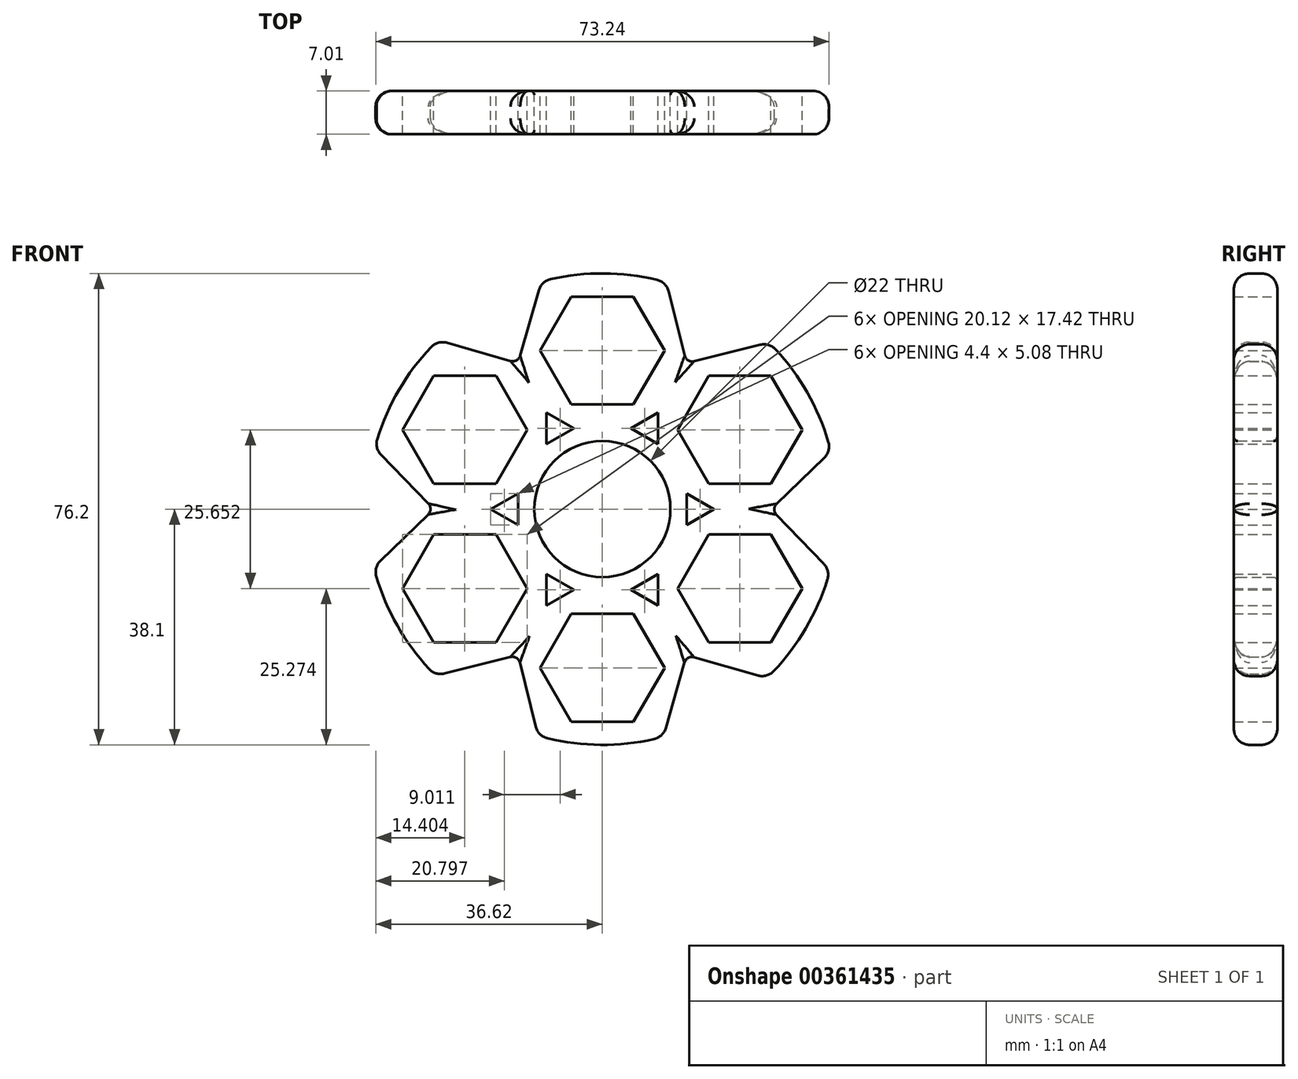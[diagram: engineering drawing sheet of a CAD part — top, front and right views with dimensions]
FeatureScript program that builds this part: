
annotation { "Feature Type Name" : "Feature", "Feature Type Description" : "" }
export const myFeature = defineFeature(function(context is Context, id is Id, definition is map)
    precondition{}
    {
        {
            var Q0;
            Q0=qCreatedBy(makeId("Front.planeOp"),FACE);
            var sketch = newSketch(context, id + "F0", { "sketchPlane" : qUnion([Q0])});
            skCircle(sketch, "E0", {"center": v(0, 0) * mm, "radius": 11 * mm});
            skCircle(sketch, "E1", {"center": v(0, 0) * mm, "radius": 38.1 * mm});
            skLineSegment(sketch, "E2", {"start": v(0, 0) * mm, "end": v(0, 19.86) * mm});
            skCircle(sketch, "E3.cCircle", {"center": v(0, 25.65) * mm, "radius": 8.71 * mm, "construction": true});
            skLineSegment(sketch, "E3.0", {"start": v(5.03, 16.94) * mm, "end": v(-5.03, 16.94) * mm});
            skLineSegment(sketch, "E3.1", {"start": v(-5.03, 16.94) * mm, "end": v(-10.06, 25.65) * mm});
            skLineSegment(sketch, "E3.2", {"start": v(-10.06, 25.65) * mm, "end": v(-5.03, 34.36) * mm});
            skLineSegment(sketch, "E3.3", {"start": v(-5.03, 34.36) * mm, "end": v(5.03, 34.36) * mm});
            skLineSegment(sketch, "E3.4", {"start": v(5.03, 34.36) * mm, "end": v(10.06, 25.65) * mm});
            skLineSegment(sketch, "E3.5", {"start": v(10.06, 25.65) * mm, "end": v(5.03, 16.94) * mm});
            skPoint(sketch, "E3.0.midPoint", {"position": v(0, 16.94) * mm});
            skLineSegment(sketch, "E4.1.0", {"start": v(-32.28, 12.83) * mm, "end": v(-27.25, 21.54) * mm});
            skLineSegment(sketch, "E4.1.1", {"start": v(-27.25, 4.11) * mm, "end": v(-32.28, 12.83) * mm});
            skLineSegment(sketch, "E4.1.2", {"start": v(-17.19, 4.11) * mm, "end": v(-27.25, 4.11) * mm});
            skLineSegment(sketch, "E4.1.3", {"start": v(-12.16, 12.83) * mm, "end": v(-17.19, 4.11) * mm});
            skLineSegment(sketch, "E4.1.4", {"start": v(-17.19, 21.54) * mm, "end": v(-12.16, 12.83) * mm});
            skCircle(sketch, "E4.1.5", {"center": v(-22.22, 12.83) * mm, "radius": 8.71 * mm, "construction": true});
            skLineSegment(sketch, "E4.1.6", {"start": v(-27.25, 21.54) * mm, "end": v(-17.19, 21.54) * mm});
            skLineSegment(sketch, "E4.2.0", {"start": v(-27.25, -21.54) * mm, "end": v(-32.28, -12.83) * mm});
            skLineSegment(sketch, "E4.2.1", {"start": v(-17.19, -21.54) * mm, "end": v(-27.25, -21.54) * mm});
            skLineSegment(sketch, "E4.2.2", {"start": v(-12.16, -12.83) * mm, "end": v(-17.19, -21.54) * mm});
            skLineSegment(sketch, "E4.2.3", {"start": v(-17.19, -4.11) * mm, "end": v(-12.16, -12.83) * mm});
            skLineSegment(sketch, "E4.2.4", {"start": v(-27.25, -4.11) * mm, "end": v(-17.19, -4.11) * mm});
            skCircle(sketch, "E4.2.5", {"center": v(-22.22, -12.83) * mm, "radius": 8.71 * mm, "construction": true});
            skLineSegment(sketch, "E4.2.6", {"start": v(-32.28, -12.83) * mm, "end": v(-27.25, -4.11) * mm});
            skLineSegment(sketch, "E5.1.3.0", {"start": v(5.03, -34.36) * mm, "end": v(-5.03, -34.36) * mm});
            skLineSegment(sketch, "E5.3.3.0", {"start": v(10.06, -25.65) * mm, "end": v(5.03, -34.36) * mm});
            skLineSegment(sketch, "E5.6.3.0", {"start": v(5.03, -16.94) * mm, "end": v(10.06, -25.65) * mm});
            skLineSegment(sketch, "E5.9.3.0", {"start": v(-5.03, -16.94) * mm, "end": v(5.03, -16.94) * mm});
            skLineSegment(sketch, "E5.12.3.0", {"start": v(-10.06, -25.65) * mm, "end": v(-5.03, -16.94) * mm});
            skCircle(sketch, "E5.15.3.0", {"center": v(0, -25.65) * mm, "radius": 8.71 * mm, "construction": true});
            skLineSegment(sketch, "E5.17.3.0", {"start": v(-5.03, -34.36) * mm, "end": v(-10.06, -25.65) * mm});
            skLineSegment(sketch, "E5.1.4.0", {"start": v(32.28, -12.83) * mm, "end": v(27.25, -21.54) * mm});
            skLineSegment(sketch, "E5.3.4.0", {"start": v(27.25, -4.11) * mm, "end": v(32.28, -12.83) * mm});
            skLineSegment(sketch, "E5.6.4.0", {"start": v(17.19, -4.11) * mm, "end": v(27.25, -4.11) * mm});
            skLineSegment(sketch, "E5.9.4.0", {"start": v(12.16, -12.83) * mm, "end": v(17.19, -4.11) * mm});
            skLineSegment(sketch, "E5.12.4.0", {"start": v(17.19, -21.54) * mm, "end": v(12.16, -12.83) * mm});
            skCircle(sketch, "E5.15.4.0", {"center": v(22.22, -12.83) * mm, "radius": 8.71 * mm, "construction": true});
            skLineSegment(sketch, "E5.17.4.0", {"start": v(27.25, -21.54) * mm, "end": v(17.19, -21.54) * mm});
            skLineSegment(sketch, "E6.1.5.0", {"start": v(27.25, 21.54) * mm, "end": v(32.28, 12.83) * mm});
            skLineSegment(sketch, "E6.3.5.0", {"start": v(17.19, 21.54) * mm, "end": v(27.25, 21.54) * mm});
            skLineSegment(sketch, "E6.6.5.0", {"start": v(12.16, 12.83) * mm, "end": v(17.19, 21.54) * mm});
            skLineSegment(sketch, "E6.9.5.0", {"start": v(17.19, 4.11) * mm, "end": v(12.16, 12.83) * mm});
            skLineSegment(sketch, "E6.12.5.0", {"start": v(27.25, 4.11) * mm, "end": v(17.19, 4.11) * mm});
            skCircle(sketch, "E6.15.5.0", {"center": v(22.22, 12.83) * mm, "radius": 8.71 * mm, "construction": true});
            skLineSegment(sketch, "E6.17.5.0", {"start": v(32.28, 12.83) * mm, "end": v(27.25, 4.11) * mm});
            skLineSegment(sketch, "E7", {"start": v(17.19, 21.54) * mm, "end": v(10.06, 25.65) * mm});
            skPoint(sketch, "E8", {"position": v(13.62, 23.6) * mm});
            skLineSegment(sketch, "E9", {"start": v(13.62, 23.6) * mm, "end": v(10.36, 36.66) * mm});
            skLineSegment(sketch, "E10", {"start": v(13.62, 23.6) * mm, "end": v(26.96, 26.92) * mm});
            skLineSegment(sketch, "E11.1.0", {"start": v(-13.62, 23.6) * mm, "end": v(-26.57, 27.3) * mm});
            skLineSegment(sketch, "E11.1.1", {"start": v(-13.62, 23.6) * mm, "end": v(-9.84, 36.8) * mm});
            skLineSegment(sketch, "E11.2.0", {"start": v(-27.25, 0) * mm, "end": v(-36.93, -9.36) * mm});
            skLineSegment(sketch, "E11.2.1", {"start": v(-27.25, 0) * mm, "end": v(-36.8, 9.88) * mm});
            skLineSegment(sketch, "E12.1.3.0", {"start": v(-13.62, -23.6) * mm, "end": v(-10.36, -36.66) * mm});
            skLineSegment(sketch, "E12.3.3.0", {"start": v(-13.62, -23.6) * mm, "end": v(-26.96, -26.92) * mm});
            skLineSegment(sketch, "E12.1.4.0", {"start": v(13.62, -23.6) * mm, "end": v(26.57, -27.3) * mm});
            skLineSegment(sketch, "E12.3.4.0", {"start": v(13.62, -23.6) * mm, "end": v(9.84, -36.8) * mm});
            skLineSegment(sketch, "E12.1.5.0", {"start": v(27.25, 0) * mm, "end": v(36.93, 9.36) * mm});
            skLineSegment(sketch, "E12.3.5.0", {"start": v(27.25, 0) * mm, "end": v(36.8, -9.88) * mm});
            skLineSegment(sketch, "E13", {"start": v(0, 0) * mm, "end": v(13.62, 23.6) * mm});
            skLineSegment(sketch, "E14", {"start": v(6.81, 11.8) * mm, "end": v(9.01, 10.53) * mm});
            skLineSegment(sketch, "E15", {"start": v(9.01, 10.53) * mm, "end": v(9.01, 15.6) * mm});
            skLineSegment(sketch, "E16.MirrorCS", {"start": v(4.61, 13.07) * mm, "end": v(9.01, 15.6) * mm});
            skLineSegment(sketch, "E17.MirrorCS", {"start": v(6.81, 11.8) * mm, "end": v(4.61, 13.07) * mm});
            skLineSegment(sketch, "E18.1.0", {"start": v(-9.01, 10.53) * mm, "end": v(-9.01, 15.6) * mm});
            skLineSegment(sketch, "E18.1.1", {"start": v(-4.61, 13.07) * mm, "end": v(-9.01, 15.6) * mm});
            skLineSegment(sketch, "E18.1.2", {"start": v(-6.81, 11.8) * mm, "end": v(-4.61, 13.07) * mm});
            skLineSegment(sketch, "E18.1.3", {"start": v(-6.81, 11.8) * mm, "end": v(-9.01, 10.53) * mm});
            skLineSegment(sketch, "E18.2.0", {"start": v(-13.62, -2.54) * mm, "end": v(-18.02, 0) * mm});
            skLineSegment(sketch, "E18.2.1", {"start": v(-13.62, 2.54) * mm, "end": v(-18.02, 0) * mm});
            skLineSegment(sketch, "E18.2.2", {"start": v(-13.62, 0) * mm, "end": v(-13.62, 2.54) * mm});
            skLineSegment(sketch, "E18.2.3", {"start": v(-13.62, 0) * mm, "end": v(-13.62, -2.54) * mm});
            skLineSegment(sketch, "E19.1.3.0", {"start": v(-4.61, -13.07) * mm, "end": v(-9.01, -15.6) * mm});
            skLineSegment(sketch, "E19.3.3.0", {"start": v(-9.01, -10.53) * mm, "end": v(-9.01, -15.6) * mm});
            skLineSegment(sketch, "E19.6.3.0", {"start": v(-6.81, -11.8) * mm, "end": v(-9.01, -10.53) * mm});
            skLineSegment(sketch, "E19.9.3.0", {"start": v(-6.81, -11.8) * mm, "end": v(-4.61, -13.07) * mm});
            skLineSegment(sketch, "E19.1.4.0", {"start": v(9.01, -10.53) * mm, "end": v(9.01, -15.6) * mm});
            skLineSegment(sketch, "E19.3.4.0", {"start": v(4.61, -13.07) * mm, "end": v(9.01, -15.6) * mm});
            skLineSegment(sketch, "E19.6.4.0", {"start": v(6.81, -11.8) * mm, "end": v(4.61, -13.07) * mm});
            skLineSegment(sketch, "E19.9.4.0", {"start": v(6.81, -11.8) * mm, "end": v(9.01, -10.53) * mm});
            skLineSegment(sketch, "E19.1.5.0", {"start": v(13.62, 2.54) * mm, "end": v(18.02, 0) * mm});
            skLineSegment(sketch, "E19.3.5.0", {"start": v(13.62, -2.54) * mm, "end": v(18.02, 0) * mm});
            skLineSegment(sketch, "E19.6.5.0", {"start": v(13.62, 0) * mm, "end": v(13.62, -2.54) * mm});
            skLineSegment(sketch, "E19.9.5.0", {"start": v(13.62, 0) * mm, "end": v(13.62, 2.54) * mm});
            skSolve(sketch);
        }
        {
            var Q0;
            Q0=makeQuery(id+"F0.imprint","IMPRINT",FACE,{"disambiguationData":[TD([[makeQuery(id+"F0.imprint","IMPRINT",EDGE,{"derivedFrom":sQuery(id+"F0.wireOp",EDGE,"E0")}),-1.0]])]});
            var Q1;
            {var subQ1=sQuery(id+"F0.wireOp",EDGE,"E3.1");Q1=makeQuery(id+"F0.imprint","IMPRINT",FACE,{"disambiguationData":[TD([[makeQuery(id+"F0.imprint","IMPRINT",EDGE,{"derivedFrom":subQ1}),1.0]])]});}
            extrude(context, id + "F1", {"entities" : qUnion([Q0, Q1]), "depth" : 7 * mm, "offsetDistance" : 25.4 * mm});
        }
        {
            var Q0;
            Q0=makeQuery(id+"F1.opExtrude","CAP_EDGE",EDGE,{"disambiguationData":[OSD([sQuery(id+"F0.wireOp",EDGE,"E11.2.1")])],"isStart":false});
            var Q1;
            {var subQ0=sQuery(id+"F0.wireOp",EDGE,"E1");Q1=makeQuery(id+"F1.opExtrude","CAP_EDGE",EDGE,{"disambiguationData":[OSD([subQ0]),TDD([makeQuery(id+"F0.imprint","IMPRINT",EDGE,{"disambiguationData":[TD([[makeQuery(id+"F0.imprint","INTERSECT",VERTEX,{"derivedFrom":[subQ0,sQuery(id+"F0.wireOp",EDGE,"E11.1.0")]}),-1.0]])],"derivedFrom":subQ0})])],"isStart":false});}
            var Q2;
            Q2=makeQuery(id+"F1.opExtrude","CAP_EDGE",EDGE,{"disambiguationData":[OSD([sQuery(id+"F0.wireOp",EDGE,"E11.1.0")])],"isStart":false});
            var Q3;
            Q3=makeQuery(id+"F1.opExtrude","CAP_EDGE",EDGE,{"disambiguationData":[OSD([sQuery(id+"F0.wireOp",EDGE,"E11.1.1")])],"isStart":false});
            var Q4;
            {var subQ0=sQuery(id+"F0.wireOp",EDGE,"E1");Q4=makeQuery(id+"F1.opExtrude","CAP_EDGE",EDGE,{"disambiguationData":[OSD([subQ0]),TDD([makeQuery(id+"F0.imprint","IMPRINT",EDGE,{"disambiguationData":[TD([[makeQuery(id+"F0.imprint","INTERSECT",VERTEX,{"derivedFrom":[subQ0,sQuery(id+"F0.wireOp",EDGE,"E9")]}),-1.0]])],"derivedFrom":subQ0})])],"isStart":false});}
            var Q5;
            Q5=makeQuery(id+"F1.opExtrude","CAP_EDGE",EDGE,{"disambiguationData":[OSD([sQuery(id+"F0.wireOp",EDGE,"E9")])],"isStart":false});
            var Q6;
            Q6=makeQuery(id+"F1.opExtrude","CAP_EDGE",EDGE,{"disambiguationData":[OSD([sQuery(id+"F0.wireOp",EDGE,"E10")])],"isStart":false});
            var Q7;
            {var subQ0=sQuery(id+"F0.wireOp",EDGE,"E1");Q7=makeQuery(id+"F1.opExtrude","CAP_EDGE",EDGE,{"disambiguationData":[OSD([subQ0]),TDD([makeQuery(id+"F0.imprint","IMPRINT",EDGE,{"disambiguationData":[TD([[makeQuery(id+"F0.imprint","INTERSECT",VERTEX,{"derivedFrom":[subQ0,sQuery(id+"F0.wireOp",EDGE,"E10")]}),1.0]])],"derivedFrom":subQ0})])],"isStart":false});}
            var Q8;
            Q8=makeQuery(id+"F1.opExtrude","CAP_EDGE",EDGE,{"disambiguationData":[OSD([sQuery(id+"F0.wireOp",EDGE,"E12.1.5.0")])],"isStart":false});
            var Q9;
            Q9=makeQuery(id+"F1.opExtrude","CAP_EDGE",EDGE,{"disambiguationData":[OSD([sQuery(id+"F0.wireOp",EDGE,"E12.3.5.0")])],"isStart":false});
            var Q10;
            {var subQ0=sQuery(id+"F0.wireOp",EDGE,"E1");Q10=makeQuery(id+"F1.opExtrude","CAP_EDGE",EDGE,{"disambiguationData":[OSD([subQ0]),TDD([makeQuery(id+"F0.imprint","IMPRINT",EDGE,{"disambiguationData":[TD([[makeQuery(id+"F0.imprint","INTERSECT",VERTEX,{"derivedFrom":[subQ0,sQuery(id+"F0.wireOp",EDGE,"E12.1.4.0")]}),-1.0]])],"derivedFrom":subQ0})])],"isStart":false});}
            var Q11;
            Q11=makeQuery(id+"F1.opExtrude","CAP_EDGE",EDGE,{"disambiguationData":[OSD([sQuery(id+"F0.wireOp",EDGE,"E12.1.4.0")])],"isStart":false});
            var Q12;
            Q12=makeQuery(id+"F1.opExtrude","CAP_EDGE",EDGE,{"disambiguationData":[OSD([sQuery(id+"F0.wireOp",EDGE,"E12.3.4.0")])],"isStart":false});
            var Q13;
            {var subQ0=sQuery(id+"F0.wireOp",EDGE,"E1");Q13=makeQuery(id+"F1.opExtrude","CAP_EDGE",EDGE,{"disambiguationData":[OSD([subQ0]),TDD([makeQuery(id+"F0.imprint","IMPRINT",EDGE,{"disambiguationData":[TD([[makeQuery(id+"F0.imprint","INTERSECT",VERTEX,{"derivedFrom":[subQ0,sQuery(id+"F0.wireOp",EDGE,"E12.1.3.0")]}),-1.0]])],"derivedFrom":subQ0})])],"isStart":false});}
            var Q14;
            Q14=makeQuery(id+"F1.opExtrude","CAP_EDGE",EDGE,{"disambiguationData":[OSD([sQuery(id+"F0.wireOp",EDGE,"E12.1.3.0")])],"isStart":false});
            var Q15;
            Q15=makeQuery(id+"F1.opExtrude","CAP_EDGE",EDGE,{"disambiguationData":[OSD([sQuery(id+"F0.wireOp",EDGE,"E12.3.3.0")])],"isStart":false});
            var Q16;
            {var subQ0=sQuery(id+"F0.wireOp",EDGE,"E1");Q16=makeQuery(id+"F1.opExtrude","CAP_EDGE",EDGE,{"disambiguationData":[OSD([subQ0]),TDD([makeQuery(id+"F0.imprint","IMPRINT",EDGE,{"disambiguationData":[TD([[makeQuery(id+"F0.imprint","INTERSECT",VERTEX,{"derivedFrom":[subQ0,sQuery(id+"F0.wireOp",EDGE,"E11.2.0")]}),-1.0]])],"derivedFrom":subQ0})])],"isStart":false});}
            var Q17;
            Q17=makeQuery(id+"F1.opExtrude","CAP_EDGE",EDGE,{"disambiguationData":[OSD([sQuery(id+"F0.wireOp",EDGE,"E11.2.0")])],"isStart":false});
            var Q18;
            {var subQ0=sQuery(id+"F0.wireOp",EDGE,"E1");Q18=makeQuery(id+"F1.opExtrude","CAP_EDGE",EDGE,{"disambiguationData":[OSD([subQ0]),TDD([makeQuery(id+"F0.imprint","IMPRINT",EDGE,{"disambiguationData":[TD([[makeQuery(id+"F0.imprint","INTERSECT",VERTEX,{"derivedFrom":[subQ0,sQuery(id+"F0.wireOp",EDGE,"E9")]}),-1.0]])],"derivedFrom":subQ0})])],"isStart":true});}
            var Q19;
            Q19=makeQuery(id+"F1.opExtrude","CAP_EDGE",EDGE,{"disambiguationData":[OSD([sQuery(id+"F0.wireOp",EDGE,"E9")])],"isStart":true});
            var Q20;
            Q20=makeQuery(id+"F1.opExtrude","CAP_EDGE",EDGE,{"disambiguationData":[OSD([sQuery(id+"F0.wireOp",EDGE,"E10")])],"isStart":true});
            var Q21;
            {var subQ0=sQuery(id+"F0.wireOp",EDGE,"E1");Q21=makeQuery(id+"F1.opExtrude","CAP_EDGE",EDGE,{"disambiguationData":[OSD([subQ0]),TDD([makeQuery(id+"F0.imprint","IMPRINT",EDGE,{"disambiguationData":[TD([[makeQuery(id+"F0.imprint","INTERSECT",VERTEX,{"derivedFrom":[subQ0,sQuery(id+"F0.wireOp",EDGE,"E10")]}),1.0]])],"derivedFrom":subQ0})])],"isStart":true});}
            var Q22;
            Q22=makeQuery(id+"F1.opExtrude","CAP_EDGE",EDGE,{"disambiguationData":[OSD([sQuery(id+"F0.wireOp",EDGE,"E12.1.5.0")])],"isStart":true});
            var Q23;
            Q23=makeQuery(id+"F1.opExtrude","CAP_EDGE",EDGE,{"disambiguationData":[OSD([sQuery(id+"F0.wireOp",EDGE,"E12.3.5.0")])],"isStart":true});
            var Q24;
            {var subQ0=sQuery(id+"F0.wireOp",EDGE,"E1");Q24=makeQuery(id+"F1.opExtrude","CAP_EDGE",EDGE,{"disambiguationData":[OSD([subQ0]),TDD([makeQuery(id+"F0.imprint","IMPRINT",EDGE,{"disambiguationData":[TD([[makeQuery(id+"F0.imprint","INTERSECT",VERTEX,{"derivedFrom":[subQ0,sQuery(id+"F0.wireOp",EDGE,"E12.1.4.0")]}),-1.0]])],"derivedFrom":subQ0})])],"isStart":true});}
            var Q25;
            Q25=makeQuery(id+"F1.opExtrude","CAP_EDGE",EDGE,{"disambiguationData":[OSD([sQuery(id+"F0.wireOp",EDGE,"E12.1.4.0")])],"isStart":true});
            var Q26;
            Q26=makeQuery(id+"F1.opExtrude","CAP_EDGE",EDGE,{"disambiguationData":[OSD([sQuery(id+"F0.wireOp",EDGE,"E12.3.4.0")])],"isStart":true});
            var Q27;
            {var subQ0=sQuery(id+"F0.wireOp",EDGE,"E1");Q27=makeQuery(id+"F1.opExtrude","CAP_EDGE",EDGE,{"disambiguationData":[OSD([subQ0]),TDD([makeQuery(id+"F0.imprint","IMPRINT",EDGE,{"disambiguationData":[TD([[makeQuery(id+"F0.imprint","INTERSECT",VERTEX,{"derivedFrom":[subQ0,sQuery(id+"F0.wireOp",EDGE,"E12.1.3.0")]}),-1.0]])],"derivedFrom":subQ0})])],"isStart":true});}
            var Q28;
            Q28=makeQuery(id+"F1.opExtrude","CAP_EDGE",EDGE,{"disambiguationData":[OSD([sQuery(id+"F0.wireOp",EDGE,"E12.1.3.0")])],"isStart":true});
            var Q29;
            Q29=makeQuery(id+"F1.opExtrude","CAP_EDGE",EDGE,{"disambiguationData":[OSD([sQuery(id+"F0.wireOp",EDGE,"E12.3.3.0")])],"isStart":true});
            var Q30;
            {var subQ0=sQuery(id+"F0.wireOp",EDGE,"E1");Q30=makeQuery(id+"F1.opExtrude","CAP_EDGE",EDGE,{"disambiguationData":[OSD([subQ0]),TDD([makeQuery(id+"F0.imprint","IMPRINT",EDGE,{"disambiguationData":[TD([[makeQuery(id+"F0.imprint","INTERSECT",VERTEX,{"derivedFrom":[subQ0,sQuery(id+"F0.wireOp",EDGE,"E11.2.0")]}),-1.0]])],"derivedFrom":subQ0})])],"isStart":true});}
            var Q31;
            Q31=makeQuery(id+"F1.opExtrude","CAP_EDGE",EDGE,{"disambiguationData":[OSD([sQuery(id+"F0.wireOp",EDGE,"E11.2.0")])],"isStart":true});
            var Q32;
            Q32=makeQuery(id+"F1.opExtrude","CAP_EDGE",EDGE,{"disambiguationData":[OSD([sQuery(id+"F0.wireOp",EDGE,"E11.2.1")])],"isStart":true});
            var Q33;
            {var subQ0=sQuery(id+"F0.wireOp",EDGE,"E1");Q33=makeQuery(id+"F1.opExtrude","CAP_EDGE",EDGE,{"disambiguationData":[OSD([subQ0]),TDD([makeQuery(id+"F0.imprint","IMPRINT",EDGE,{"disambiguationData":[TD([[makeQuery(id+"F0.imprint","INTERSECT",VERTEX,{"derivedFrom":[subQ0,sQuery(id+"F0.wireOp",EDGE,"E11.1.0")]}),-1.0]])],"derivedFrom":subQ0})])],"isStart":true});}
            var Q34;
            Q34=makeQuery(id+"F1.opExtrude","CAP_EDGE",EDGE,{"disambiguationData":[OSD([sQuery(id+"F0.wireOp",EDGE,"E11.1.0")])],"isStart":true});
            var Q35;
            Q35=makeQuery(id+"F1.opExtrude","CAP_EDGE",EDGE,{"disambiguationData":[OSD([sQuery(id+"F0.wireOp",EDGE,"E11.1.1")])],"isStart":true});
            var Q36;
            Q36=makeQuery(id+"F1.opExtrude","SWEPT_EDGE",EDGE,{"disambiguationData":[OSD([sQuery(id+"F0.wireOp",EDGE,"E1"),sQuery(id+"F0.wireOp",EDGE,"E12.1.5.0")])]});
            var Q37;
            Q37=makeQuery(id+"F1.opExtrude","SWEPT_EDGE",EDGE,{"disambiguationData":[OSD([sQuery(id+"F0.wireOp",EDGE,"E1"),sQuery(id+"F0.wireOp",EDGE,"E10")])]});
            var Q38;
            Q38=makeQuery(id+"F1.opExtrude","SWEPT_EDGE",EDGE,{"disambiguationData":[OSD([sQuery(id+"F0.wireOp",EDGE,"E1"),sQuery(id+"F0.wireOp",EDGE,"E9")])]});
            var Q39;
            Q39=makeQuery(id+"F1.opExtrude","SWEPT_EDGE",EDGE,{"disambiguationData":[OSD([sQuery(id+"F0.wireOp",EDGE,"E1"),sQuery(id+"F0.wireOp",EDGE,"E11.1.1")])]});
            var Q40;
            Q40=makeQuery(id+"F1.opExtrude","SWEPT_EDGE",EDGE,{"disambiguationData":[OSD([sQuery(id+"F0.wireOp",EDGE,"E1"),sQuery(id+"F0.wireOp",EDGE,"E11.1.0")])]});
            var Q41;
            Q41=makeQuery(id+"F1.opExtrude","SWEPT_EDGE",EDGE,{"disambiguationData":[OSD([sQuery(id+"F0.wireOp",EDGE,"E1"),sQuery(id+"F0.wireOp",EDGE,"E11.2.1")])]});
            var Q42;
            Q42=makeQuery(id+"F1.opExtrude","SWEPT_EDGE",EDGE,{"disambiguationData":[OSD([sQuery(id+"F0.wireOp",EDGE,"E1"),sQuery(id+"F0.wireOp",EDGE,"E11.2.0")])]});
            var Q43;
            Q43=makeQuery(id+"F1.opExtrude","SWEPT_EDGE",EDGE,{"disambiguationData":[OSD([sQuery(id+"F0.wireOp",EDGE,"E1"),sQuery(id+"F0.wireOp",EDGE,"E12.3.3.0")])]});
            var Q44;
            Q44=makeQuery(id+"F1.opExtrude","SWEPT_EDGE",EDGE,{"disambiguationData":[OSD([sQuery(id+"F0.wireOp",EDGE,"E1"),sQuery(id+"F0.wireOp",EDGE,"E12.1.3.0")])]});
            var Q45;
            Q45=makeQuery(id+"F1.opExtrude","SWEPT_EDGE",EDGE,{"disambiguationData":[OSD([sQuery(id+"F0.wireOp",EDGE,"E1"),sQuery(id+"F0.wireOp",EDGE,"E12.3.4.0")])]});
            var Q46;
            Q46=makeQuery(id+"F1.opExtrude","SWEPT_EDGE",EDGE,{"disambiguationData":[OSD([sQuery(id+"F0.wireOp",EDGE,"E1"),sQuery(id+"F0.wireOp",EDGE,"E12.1.4.0")])]});
            var Q47;
            Q47=makeQuery(id+"F1.opExtrude","SWEPT_EDGE",EDGE,{"disambiguationData":[OSD([sQuery(id+"F0.wireOp",EDGE,"E1"),sQuery(id+"F0.wireOp",EDGE,"E12.3.5.0")])]});
            fillet(context, id + "F2", {"entities" : qUnion([Q0, Q1, Q2, Q3, Q4, Q5, Q6, Q7, Q8, Q9, Q10, Q11, Q12, Q13, Q14, Q15, Q16, Q17, Q18, Q19, Q20, Q21, Q22, Q23, Q24, Q25, Q26, Q27, Q28, Q29, Q30, Q31, Q32, Q33, Q34, Q35, Q36, Q37, Q38, Q39, Q40, Q41, Q42, Q43, Q44, Q45, Q46, Q47]), "radius" : 2.54 * mm, "tangentPropagation" : true, "allowEdgeOverflow" : false});
        }
        {
            var Q0;
            Q0=makeQuery(id+"F2.opFillet","BLEND_EDGE",EDGE,{"blendedFrom":[makeQuery(id+"F1.opExtrude","CAP_EDGE",EDGE,{"disambiguationData":[OSD([sQuery(id+"F0.wireOp",EDGE,"E11.1.0")])],"isStart":false}),makeQuery(id+"F1.opExtrude","CAP_EDGE",EDGE,{"disambiguationData":[OSD([sQuery(id+"F0.wireOp",EDGE,"E11.1.1")])],"isStart":false})],"blendedInto":[]});
            var Q1;
            Q1=makeQuery(id+"F2.opFillet","BLEND_EDGE",EDGE,{"blendedFrom":[makeQuery(id+"F1.opExtrude","CAP_EDGE",EDGE,{"disambiguationData":[OSD([sQuery(id+"F0.wireOp",EDGE,"E9")])],"isStart":false}),makeQuery(id+"F1.opExtrude","CAP_EDGE",EDGE,{"disambiguationData":[OSD([sQuery(id+"F0.wireOp",EDGE,"E10")])],"isStart":false})],"blendedInto":[]});
            var Q2;
            Q2=makeQuery(id+"F2.opFillet","BLEND_EDGE",EDGE,{"blendedFrom":[makeQuery(id+"F1.opExtrude","CAP_EDGE",EDGE,{"disambiguationData":[OSD([sQuery(id+"F0.wireOp",EDGE,"E12.1.5.0")])],"isStart":false}),makeQuery(id+"F1.opExtrude","CAP_EDGE",EDGE,{"disambiguationData":[OSD([sQuery(id+"F0.wireOp",EDGE,"E12.3.5.0")])],"isStart":false})],"blendedInto":[]});
            var Q3;
            Q3=makeQuery(id+"F2.opFillet","BLEND_EDGE",EDGE,{"blendedFrom":[makeQuery(id+"F1.opExtrude","CAP_EDGE",EDGE,{"disambiguationData":[OSD([sQuery(id+"F0.wireOp",EDGE,"E12.1.4.0")])],"isStart":false}),makeQuery(id+"F1.opExtrude","CAP_EDGE",EDGE,{"disambiguationData":[OSD([sQuery(id+"F0.wireOp",EDGE,"E12.3.4.0")])],"isStart":false})],"blendedInto":[]});
            var Q4;
            Q4=makeQuery(id+"F2.opFillet","BLEND_EDGE",EDGE,{"blendedFrom":[makeQuery(id+"F1.opExtrude","CAP_EDGE",EDGE,{"disambiguationData":[OSD([sQuery(id+"F0.wireOp",EDGE,"E12.1.3.0")])],"isStart":false}),makeQuery(id+"F1.opExtrude","CAP_EDGE",EDGE,{"disambiguationData":[OSD([sQuery(id+"F0.wireOp",EDGE,"E12.3.3.0")])],"isStart":false})],"blendedInto":[]});
            var Q5;
            Q5=makeQuery(id+"F2.opFillet","BLEND_EDGE",EDGE,{"blendedFrom":[makeQuery(id+"F1.opExtrude","CAP_EDGE",EDGE,{"disambiguationData":[OSD([sQuery(id+"F0.wireOp",EDGE,"E11.2.0")])],"isStart":false}),makeQuery(id+"F1.opExtrude","CAP_EDGE",EDGE,{"disambiguationData":[OSD([sQuery(id+"F0.wireOp",EDGE,"E11.2.1")])],"isStart":false})],"blendedInto":[]});
            fillet(context, id + "F3", {"entities" : qUnion([Q0, Q1, Q2, Q3, Q4, Q5]), "radius" : 1.27 * mm, "tangentPropagation" : true, "allowEdgeOverflow" : false});
        }
        {
            var Q0;
            Q0=makeQuery(id+"F1.opExtrude","CAP_EDGE",EDGE,{"disambiguationData":[OSD([sQuery(id+"F0.wireOp",EDGE,"E0")])],"isStart":false});
            var Q1;
            Q1=makeQuery(id+"F1.opExtrude","CAP_EDGE",EDGE,{"disambiguationData":[OSD([sQuery(id+"F0.wireOp",EDGE,"E0")])],"isStart":true});
            fillet(context, id + "F4", {"entities" : qUnion([Q0, Q1]), "radius" : 0.64 * mm, "tangentPropagation" : true, "allowEdgeOverflow" : false});
        }
    });
